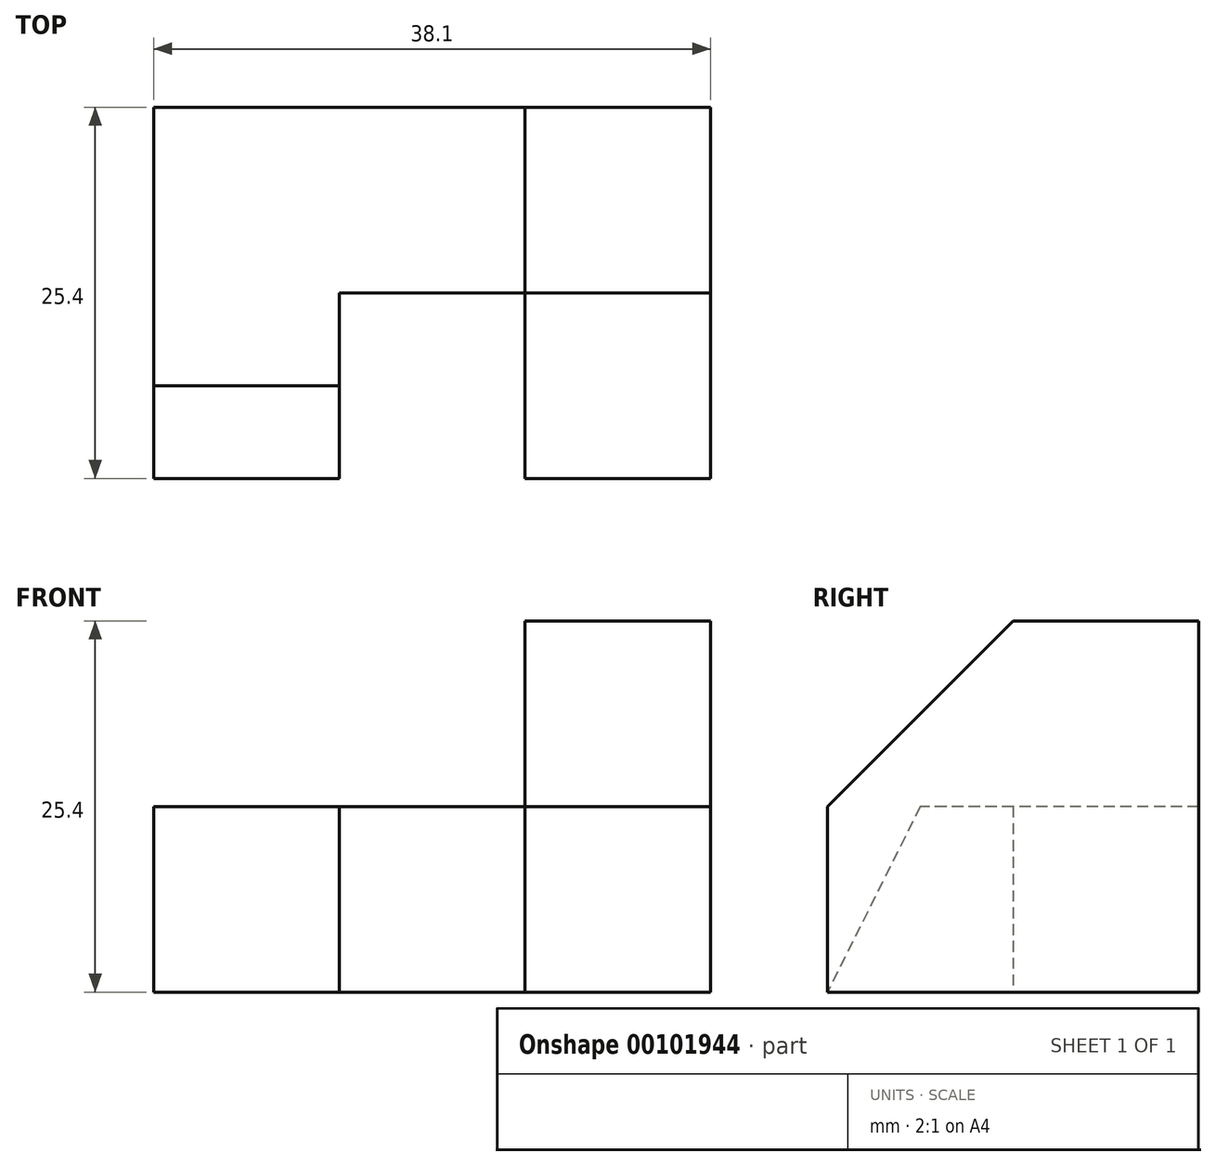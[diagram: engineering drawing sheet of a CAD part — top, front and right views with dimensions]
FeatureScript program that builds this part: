
annotation { "Feature Type Name" : "Feature", "Feature Type Description" : "" }
export const myFeature = defineFeature(function(context is Context, id is Id, definition is map)
    precondition{}
    {
        {
            var Q0;
            Q0=qCreatedBy(makeId("Right.planeOp"),FACE);
            var sketch = newSketch(context, id + "F0", { "sketchPlane" : qUnion([Q0])});
            skLineSegment(sketch, "E0", {"start": v(0, 0) * mm, "end": v(-25.4, 0) * mm});
            skLineSegment(sketch, "E1", {"start": v(-25.4, 0) * mm, "end": v(-25.4, 25.4) * mm});
            skLineSegment(sketch, "E2", {"start": v(-25.4, 25.4) * mm, "end": v(0, 25.4) * mm});
            skLineSegment(sketch, "E3", {"start": v(0, 25.4) * mm, "end": v(0, 0) * mm});
            skSolve(sketch);
        }
        {
            var Q0;
            Q0 = qSketchRegion(id + "F0", true);
            extrude(context, id + "F1", {"entities" : qUnion([Q0]), "endBound" : BoundingType.SYMMETRIC, "depth" : 38.1 * mm});
        }
        {
            var Q0;
            Q0=makeQuery(id+"F1.opExtrude","CAP_FACE",FACE,{"disambiguationData":[OSD([sQuery(id+"F0.wireOp",EDGE,"E0"),sQuery(id+"F0.wireOp",EDGE,"E1"),sQuery(id+"F0.wireOp",EDGE,"E2"),sQuery(id+"F0.wireOp",EDGE,"E3")])],"isStart":false});
            var sketch = newSketch(context, id + "F2", { "sketchPlane" : qUnion([Q0])});
            skLineSegment(sketch, "E4", {"start": v(-25.4, 12.7) * mm, "end": v(-12.7, 25.4) * mm});
            skSolve(sketch);
        }
        {
            var Q0;
            {var subQ0=sQuery(id+"F2.wireOp",EDGE,"E4");Q0=makeQuery(id+"F2.imprint","IMPRINT",FACE,{"disambiguationData":[TD([[makeQuery(id+"F2.imprint","IMPRINT",EDGE,{"derivedFrom":subQ0}),1.0]])]});}
            extrude(context, id + "F3", {"entities" : qUnion([Q0]), "operationType" : NewBodyOperationType.REMOVE, "oppositeDirection" : true, "depth" : 12.7 * mm});
        }
        {
            var Q0;
            Q0=makeQuery(id+"F1.opExtrude","SWEPT_FACE",FACE,{"disambiguationData":[OSD([sQuery(id+"F0.wireOp",EDGE,"E1")])]});
            var sketch = newSketch(context, id + "F4", { "sketchPlane" : qUnion([Q0])});
            skLineSegment(sketch, "E5.bottom", {"start": v(-19.05, 25.4) * mm, "end": v(6.35, 25.4) * mm});
            skLineSegment(sketch, "E5.top", {"start": v(-19.05, 12.7) * mm, "end": v(6.35, 12.7) * mm});
            skLineSegment(sketch, "E5.left", {"start": v(-19.05, 25.4) * mm, "end": v(-19.05, 12.7) * mm});
            skLineSegment(sketch, "E5.right", {"start": v(6.35, 25.4) * mm, "end": v(6.35, 12.7) * mm});
            skSolve(sketch);
        }
        {
            var Q0;
            Q0=makeQuery(id+"F4.imprint","IMPRINT",FACE,{"disambiguationData":[TD([[makeQuery(id+"F4.imprint","IMPRINT",EDGE,{"derivedFrom":sQuery(id+"F4.wireOp",EDGE,"E5.bottom")}),1.0]])]});
            extrude(context, id + "F5", {"entities" : qUnion([Q0]), "operationType" : NewBodyOperationType.REMOVE, "endBound" : BoundingType.THROUGH_ALL, "oppositeDirection" : true, "depth" : 25.4 * mm});
        }
        {
            var Q0;
            Q0=makeQuery(id+"F1.opExtrude","SWEPT_FACE",FACE,{"disambiguationData":[OSD([sQuery(id+"F0.wireOp",EDGE,"E1")])]});
            var sketch = newSketch(context, id + "F6", { "sketchPlane" : qUnion([Q0])});
            skLineSegment(sketch, "E6.bottom", {"start": v(6.35, 12.7) * mm, "end": v(-6.35, 12.7) * mm});
            skLineSegment(sketch, "E6.top", {"start": v(6.35, 0) * mm, "end": v(-6.35, 0) * mm});
            skLineSegment(sketch, "E6.left", {"start": v(6.35, 12.7) * mm, "end": v(6.35, 0) * mm});
            skLineSegment(sketch, "E6.right", {"start": v(-6.35, 12.7) * mm, "end": v(-6.35, 0) * mm});
            skSolve(sketch);
        }
        {
            var Q0;
            Q0=makeQuery(id+"F6.imprint","IMPRINT",FACE,{"disambiguationData":[TD([[makeQuery(id+"F6.imprint","IMPRINT",EDGE,{"derivedFrom":sQuery(id+"F6.wireOp",EDGE,"E6.bottom")}),-1.0]])]});
            extrude(context, id + "F7", {"entities" : qUnion([Q0]), "operationType" : NewBodyOperationType.REMOVE, "oppositeDirection" : true, "depth" : 12.7 * mm});
        }
        {
            var Q0;
            Q0=makeQuery(id+"F7.boolean.opBoolean","COPY",FACE,{"derivedFrom":makeQuery(id+"F7.opExtrude","SWEPT_FACE",FACE,{"disambiguationData":[OSD([sQuery(id+"F6.wireOp",EDGE,"E6.right")])]})});
            var sketch = newSketch(context, id + "F8", { "sketchPlane" : qUnion([Q0])});
            skLineSegment(sketch, "E7", {"start": v(-19.05, 12.7) * mm, "end": v(-25.4, 0) * mm});
            skSolve(sketch);
        }
        {
            var Q0;
            {var subQ0=sQuery(id+"F8.wireOp",EDGE,"E7");Q0=makeQuery(id+"F8.imprint","IMPRINT",FACE,{"disambiguationData":[TD([[makeQuery(id+"F8.imprint","IMPRINT",EDGE,{"derivedFrom":subQ0}),-1.0]])]});}
            extrude(context, id + "F9", {"entities" : qUnion([Q0]), "operationType" : NewBodyOperationType.REMOVE, "endBound" : BoundingType.THROUGH_ALL, "oppositeDirection" : true, "depth" : 25.4 * mm});
        }
    });
